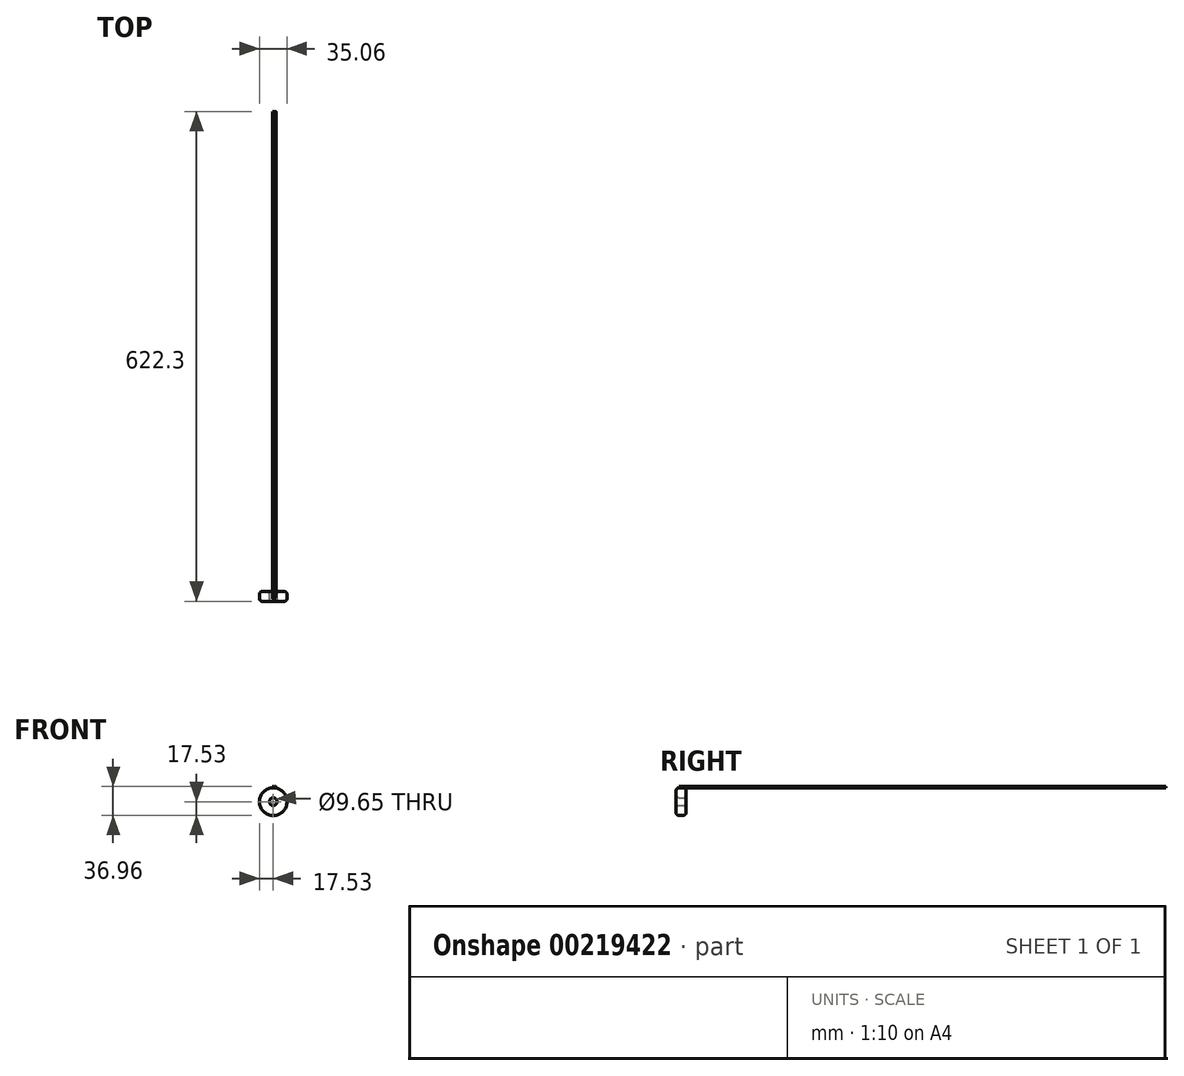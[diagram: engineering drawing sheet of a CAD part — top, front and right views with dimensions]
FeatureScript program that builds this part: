
annotation { "Feature Type Name" : "Feature", "Feature Type Description" : "" }
export const myFeature = defineFeature(function(context is Context, id is Id, definition is map)
    precondition{}
    {
        {
            assignVariable(context, id + "F0", {"variableType" : VariableType.LENGTH, "name" : "ToroidThk", "lengthValue" : 12.7 * mm});
        }
        {
            var Q0;
            Q0=qCreatedBy(makeId("Front.planeOp"),FACE);
            var sketch = newSketch(context, id + "F1", { "sketchPlane" : qUnion([Q0])});
            skCircle(sketch, "E0", {"center": v(0, 0) * mm, "radius": 17.53 * mm});
            skCircle(sketch, "E1", {"center": v(0, 0) * mm, "radius": 4.83 * mm});
            skSolve(sketch);
        }
        {
            var Q0;
            Q0=makeQuery(id+"F1.imprint","IMPRINT",FACE,{"disambiguationData":[TD([[makeQuery(id+"F1.imprint","IMPRINT",EDGE,{"derivedFrom":sQuery(id+"F1.wireOp",EDGE,"E0")}),1.0]])]});
            extrude(context, id + "F2", {"entities" : qUnion([Q0]), "depth" : getVariable(context, 'ToroidThk'), "offsetDistance" : 25.4 * mm});
        }
        {
            var Q0;
            Q0=makeQuery(id+"F2.opExtrude","CAP_EDGE",EDGE,{"disambiguationData":[OSD([sQuery(id+"F1.wireOp",EDGE,"E0")])],"isStart":false});
            var Q1;
            Q1=makeQuery(id+"F2.opExtrude","CAP_EDGE",EDGE,{"disambiguationData":[OSD([sQuery(id+"F1.wireOp",EDGE,"E0")])],"isStart":true});
            var Q2;
            Q2=makeQuery(id+"F2.opExtrude","CAP_EDGE",EDGE,{"disambiguationData":[OSD([sQuery(id+"F1.wireOp",EDGE,"E1")])],"isStart":true});
            var Q3;
            Q3=makeQuery(id+"F2.opExtrude","CAP_EDGE",EDGE,{"disambiguationData":[OSD([sQuery(id+"F1.wireOp",EDGE,"E1")])],"isStart":false});
            fillet(context, id + "F3", {"entities" : qUnion([Q0, Q1, Q2, Q3]), "tangentPropagation" : true, "radius" : 3.8 * mm, "defaultsChanged" : true, "vertexSettings" : [], "allowEdgeOverflow" : false});
        }
        {
            var Q0;
            Q0=qCreatedBy(makeId("Front.planeOp"), FACE);
            var sketch = newSketch(context, id + "F4", { "sketchPlane" : qUnion([Q0])});
            skCircle(sketch, "E2", {"center": v(0, 18.54) * mm, "radius": 0.89 * mm});
            skCircle(sketch, "E3", {"center": v(2.54, 18.54) * mm, "radius": 0.89 * mm});
            skSolve(sketch);
        }
        {
            var Q0;
            Q0 = qSketchRegion(id + "F4", true);
            extrude(context, id + "F5", {"entities" : qUnion([Q0]), "domain" : OperationDomain.MODEL, "flatOperationType" : FlatOperationType.REMOVE, "depth" : 8.64 * mm, "offsetDistance" : 25.4 * mm, "hasSecondDirection" : true, "secondDirectionOppositeDirection" : true, "secondDirectionDepth" : 609.6 * mm});
        }
    });
